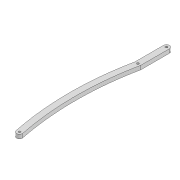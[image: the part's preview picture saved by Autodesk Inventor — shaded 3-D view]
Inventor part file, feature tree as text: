
AUTODESK INVENTOR PART (.ipt)
format: ipt  version: 2022 (Build 260153000, 153)  size: 99,328 bytes
history: native  units: mm
features: extrude x1, sketch x1
ambient origin geometry x8: Origin, YZ Plane, XZ Plane, XY Plane, X Axis, Y Axis, Z Axis, Center Point
bodies: Solid1 (feature_tree)
feature tree (2):
  extrude  "Extrusion1"  Depth=300.0mm
  sketch  "Sketch1"  dims[d0=2.2mm d1=2.2mm d2=6.0mm d3=149.325mm d6=4.0mm d7=0.0mm d14=2.2mm d15=120.259mm d16=300.0mm d17=300.0mm]
